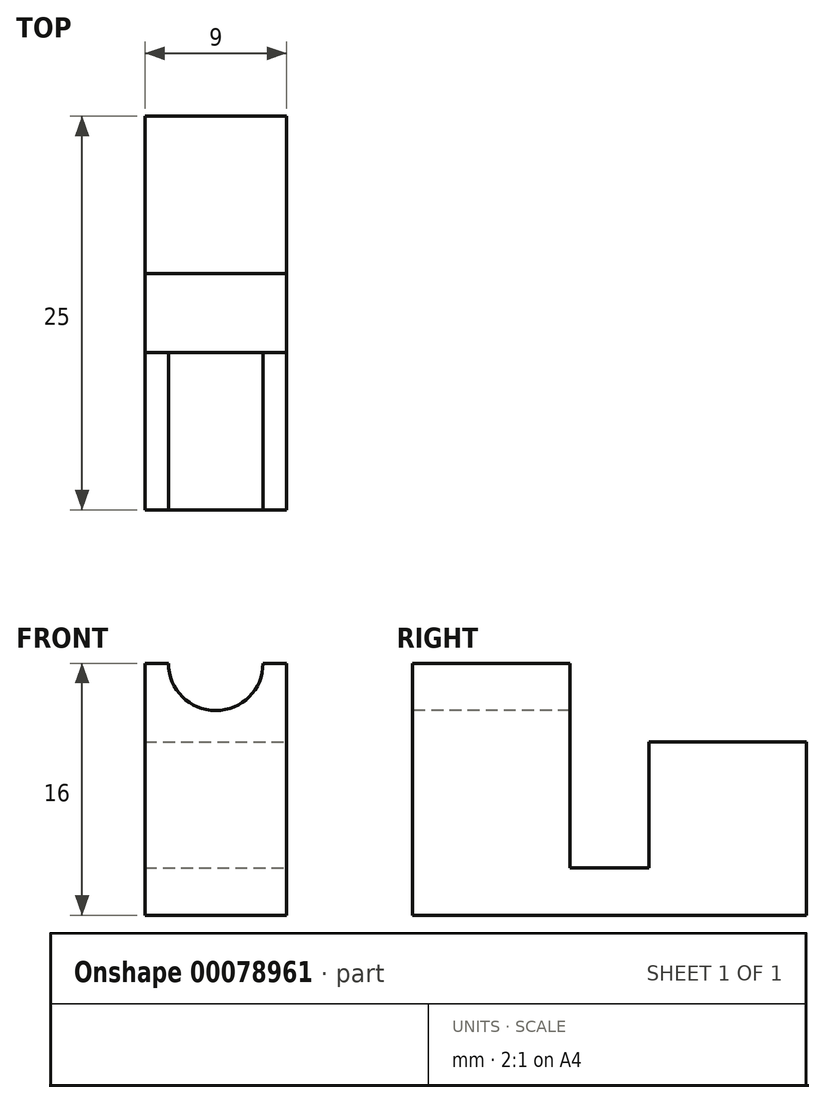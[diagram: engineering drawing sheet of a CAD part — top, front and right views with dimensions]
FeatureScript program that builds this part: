
annotation { "Feature Type Name" : "Feature", "Feature Type Description" : "" }
export const myFeature = defineFeature(function(context is Context, id is Id, definition is map)
    precondition{}
    {
        {
            var Q0;
            Q0=qCreatedBy(makeId("Top.planeOp"),FACE);
            var sketch = newSketch(context, id + "F0", { "sketchPlane" : qUnion([Q0])});
            skLineSegment(sketch, "E0.bottom", {"start": v(0, 0) * mm, "end": v(9, 0) * mm});
            skLineSegment(sketch, "E0.top", {"start": v(0, 10) * mm, "end": v(9, 10) * mm});
            skLineSegment(sketch, "E0.left", {"start": v(0, 0) * mm, "end": v(0, 10) * mm});
            skLineSegment(sketch, "E0.right", {"start": v(9, 0) * mm, "end": v(9, 10) * mm});
            skSolve(sketch);
        }
        {
            var Q0;
            Q0=makeQuery(id+"F0.imprint","IMPRINT",FACE,{"disambiguationData":[TD([[makeQuery(id+"F0.imprint","IMPRINT",EDGE,{"derivedFrom":sQuery(id+"F0.wireOp",EDGE,"E0.bottom")}),1.0]])]});
            extrude(context, id + "F1", {"entities" : qUnion([Q0]), "depth" : 13 * mm});
        }
        {
            var Q0;
            Q0=makeQuery(id+"F1.opExtrude","SWEPT_FACE",FACE,{"disambiguationData":[OSD([sQuery(id+"F0.wireOp",EDGE,"E0.bottom")])]});
            var sketch = newSketch(context, id + "F2", { "sketchPlane" : qUnion([Q0])});
            skLineSegment(sketch, "E1", {"start": v(0, 0) * mm, "end": v(0, 13) * mm, "construction": true});
            skLineSegment(sketch, "E2", {"start": v(0, 13) * mm, "end": v(9, 13) * mm, "construction": true});
            skCircle(sketch, "E3", {"center": v(4.5, 13) * mm, "radius": 3 * mm});
            skSolve(sketch);
        }
        {
            var Q0;
            {var subQ0=sQuery(id+"F2.wireOp",EDGE,"E3");var subQ1=makeQuery(id+"F1.opExtrude","CAP_EDGE",EDGE,{"disambiguationData":[OSD([sQuery(id+"F0.wireOp",EDGE,"E0.bottom")])],"isStart":true});var subQ2=makeQuery(id+"F2.imprint","INTERSECT",VERTEX,{"disambiguationData":[OD(0.0)],"derivedFrom":[subQ1,subQ0]});Q0=makeQuery(id+"F2.imprint","IMPRINT",FACE,{"disambiguationData":[TD([[makeQuery(id+"F2.imprint","IMPRINT",EDGE,{"disambiguationData":[TD([[subQ2,1.0]])],"derivedFrom":subQ0}),1.0]])]});}
            var Q1;
            {var subQ0=sQuery(id+"F2.wireOp",EDGE,"E3");var subQ1=makeQuery(id+"F1.opExtrude","CAP_EDGE",EDGE,{"disambiguationData":[OSD([sQuery(id+"F0.wireOp",EDGE,"E0.bottom")])],"isStart":false});var subQ2=makeQuery(id+"F2.imprint","INTERSECT",VERTEX,{"disambiguationData":[OD(0.0)],"derivedFrom":[subQ1,subQ0]});Q1=makeQuery(id+"F2.imprint","IMPRINT",FACE,{"disambiguationData":[TD([[makeQuery(id+"F2.imprint","IMPRINT",EDGE,{"disambiguationData":[TD([[subQ2,-1.0]])],"derivedFrom":subQ0}),1.0]])]});}
            extrude(context, id + "F3", {"entities" : qUnion([Q0, Q1]), "operationType" : NewBodyOperationType.REMOVE, "oppositeDirection" : true, "depth" : 25 * mm});
        }
        {
            var Q0;
            Q0=makeQuery(id+"F1.opExtrude","CAP_FACE",FACE,{"disambiguationData":[OSD([sQuery(id+"F0.wireOp",EDGE,"E0.bottom"),sQuery(id+"F0.wireOp",EDGE,"E0.top"),sQuery(id+"F0.wireOp",EDGE,"E0.left"),sQuery(id+"F0.wireOp",EDGE,"E0.right")])],"isStart":true});
            var sketch = newSketch(context, id + "F4", { "sketchPlane" : qUnion([Q0])});
            skLineSegment(sketch, "E4.bottom", {"start": v(0, 0) * mm, "end": v(9, 0) * mm});
            skLineSegment(sketch, "E4.top", {"start": v(0, -25) * mm, "end": v(9, -25) * mm});
            skLineSegment(sketch, "E4.left", {"start": v(0, 0) * mm, "end": v(0, -25) * mm});
            skLineSegment(sketch, "E4.right", {"start": v(9, 0) * mm, "end": v(9, -25) * mm});
            skSolve(sketch);
        }
        {
            var Q0;
            {var subQ0=sQuery(id+"F4.wireOp",EDGE,"E4.bottom");Q0=makeQuery(id+"F4.imprint","IMPRINT",FACE,{"disambiguationData":[TD([[makeQuery(id+"F4.imprint","IMPRINT",EDGE,{"derivedFrom":subQ0}),-1.0]])]});}
            var Q1;
            {var subQ0=sQuery(id+"F4.wireOp",EDGE,"E4.top");Q1=makeQuery(id+"F4.imprint","IMPRINT",FACE,{"disambiguationData":[TD([[makeQuery(id+"F4.imprint","IMPRINT",EDGE,{"derivedFrom":subQ0}),1.0]])]});}
            extrude(context, id + "F5", {"entities" : qUnion([Q0, Q1]), "operationType" : NewBodyOperationType.ADD, "depth" : 3 * mm});
        }
        {
            var Q0;
            Q0=makeQuery(id+"F5.opExtrude","CAP_FACE",FACE,{"disambiguationData":[OSD([sQuery(id+"F4.wireOp",EDGE,"E4.bottom"),sQuery(id+"F4.wireOp",EDGE,"E4.top"),sQuery(id+"F4.wireOp",EDGE,"E4.left"),sQuery(id+"F4.wireOp",EDGE,"E4.right")])],"isStart":true});
            var sketch = newSketch(context, id + "F6", { "sketchPlane" : qUnion([Q0])});
            skLineSegment(sketch, "E5.bottom", {"start": v(0, 25) * mm, "end": v(9, 25) * mm});
            skLineSegment(sketch, "E5.top", {"start": v(0, 15) * mm, "end": v(9, 15) * mm});
            skLineSegment(sketch, "E5.left", {"start": v(0, 25) * mm, "end": v(0, 15) * mm});
            skLineSegment(sketch, "E5.right", {"start": v(9, 25) * mm, "end": v(9, 15) * mm});
            skSolve(sketch);
        }
        {
            var Q0;
            Q0=makeQuery(id+"F6.imprint","IMPRINT",FACE,{"disambiguationData":[TD([[makeQuery(id+"F6.imprint","IMPRINT",EDGE,{"derivedFrom":sQuery(id+"F6.wireOp",EDGE,"E5.bottom")}),-1.0]])]});
            extrude(context, id + "F7", {"entities" : qUnion([Q0]), "operationType" : NewBodyOperationType.ADD, "depth" : 8 * mm});
        }
    });
